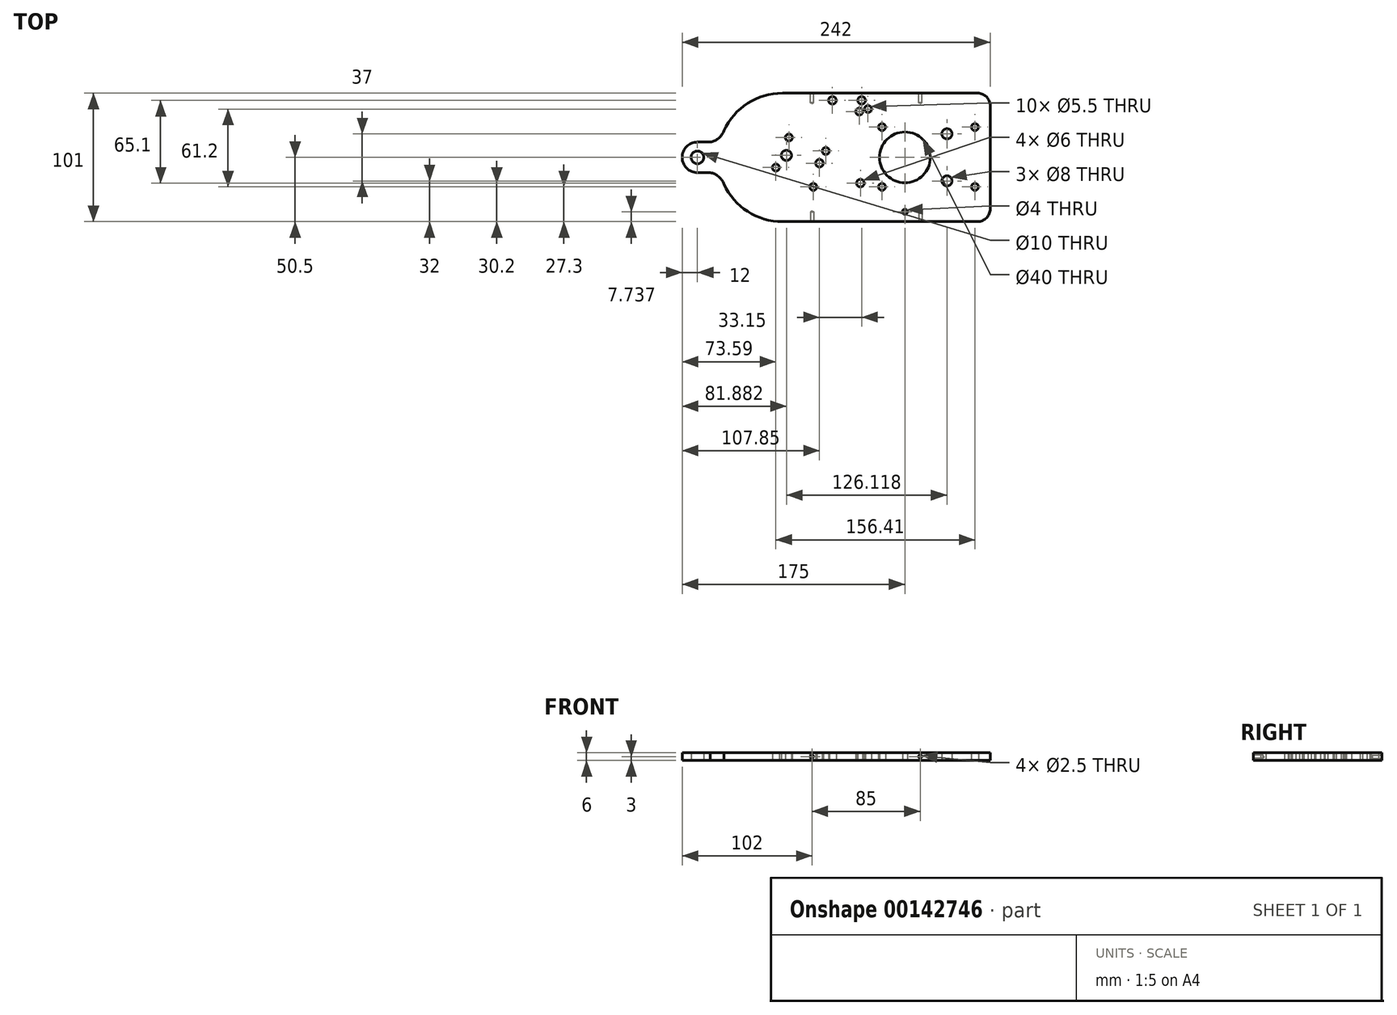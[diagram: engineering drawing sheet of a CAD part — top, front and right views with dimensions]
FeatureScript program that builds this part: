
annotation { "Feature Type Name" : "Feature", "Feature Type Description" : "" }
export const myFeature = defineFeature(function(context is Context, id is Id, definition is map)
    precondition{}
    {
        {
            var Q0;
            Q0=qCreatedBy(makeId("Top.planeOp"),FACE);
            var sketch = newSketch(context, id + "F0", { "sketchPlane" : qUnion([Q0])});
            skCircle(sketch, "E0", {"center": v(0, 0) * mm, "radius": 20 * mm});
            skLineSegment(sketch, "E1.bottom", {"start": v(-96.28, 50.5) * mm, "end": v(57, 50.5) * mm});
            skLineSegment(sketch, "E1.top", {"start": v(-96.28, -50.5) * mm, "end": v(57, -50.5) * mm});
            skLineSegment(sketch, "E1.right", {"start": v(67, 40.5) * mm, "end": v(67, -40.5) * mm});
            skLineSegment(sketch, "E2", {"start": v(-125.63, 0) * mm, "end": v(368.6, 0) * mm, "construction": true});
            skArc(sketch, "E3", {"start": v(-163, 12) * mm, "mid": v(-175, 0) * mm, "end": v(-163, -12) * mm});
            skArc(sketch, "E4", {"start": v(-96.28, 50.5) * mm, "mid": v(-124.3, 42.01) * mm, "end": v(-142.9, 19.41) * mm});
            skLineSegment(sketch, "E5", {"start": v(-163, 0) * mm, "end": v(-153.8, 0) * mm, "construction": true});
            skLineSegment(sketch, "E6", {"start": v(-163, 12) * mm, "end": v(-153, 12) * mm});
            skLineSegment(sketch, "E7", {"start": v(-163, -12) * mm, "end": v(-153, -12) * mm});
            skArc(sketch, "E8", {"start": v(-153, 12) * mm, "mid": v(-146.39, 15.05) * mm, "end": v(-142.2, 21) * mm});
            skArc(sketch, "E9.MirrorCS", {"start": v(-153, -12) * mm, "mid": v(-146.39, -15.05) * mm, "end": v(-142.2, -21) * mm});
            skPoint(sketch, "E10.visualSharp", {"position": v(67, 50.5) * mm});
            skArc(sketch, "E10.filletArc", {"start": v(67, 40.5) * mm, "mid": v(64.07, 47.57) * mm, "end": v(57, 50.5) * mm});
            skPoint(sketch, "E11.visualSharp", {"position": v(67, -50.5) * mm});
            skArc(sketch, "E11.filletArc", {"start": v(57, -50.5) * mm, "mid": v(64.07, -47.57) * mm, "end": v(67, -40.5) * mm});
            skArc(sketch, "E12.trimOffspring", {"start": v(-142.9, -19.41) * mm, "mid": v(-124.3, -42.01) * mm, "end": v(-96.28, -50.5) * mm});
            skCircle(sketch, "E13", {"center": v(-163, 0) * mm, "radius": 5 * mm});
            skCircle(sketch, "E14", {"center": v(33, -18.5) * mm, "radius": 4 * mm});
            skCircle(sketch, "E15", {"center": v(33, 18.5) * mm, "radius": 4 * mm});
            skCircle(sketch, "E16", {"center": v(-57, 44.8) * mm, "radius": 3 * mm});
            skCircle(sketch, "E17", {"center": v(-34, 44.8) * mm, "radius": 3 * mm});
            skCircle(sketch, "E18", {"center": v(-67.15, -4.55) * mm, "radius": 3 * mm});
            skLineSegment(sketch, "E19", {"start": v(0, 0) * mm, "end": v(0, -42.76) * mm, "construction": true});
            skCircle(sketch, "E20", {"center": v(55, 23.8) * mm, "radius": 2.75 * mm});
            skCircle(sketch, "E21", {"center": v(55, -23.2) * mm, "radius": 2.75 * mm});
            skCircle(sketch, "E22", {"center": v(-35.9, 36) * mm, "radius": 2.75 * mm});
            skCircle(sketch, "E23", {"center": v(-29, 38) * mm, "radius": 2.75 * mm});
            skCircle(sketch, "E24", {"center": v(-62.2, 5) * mm, "radius": 2.75 * mm});
            skCircle(sketch, "E25", {"center": v(-91.15, 15.6) * mm, "radius": 2.75 * mm});
            skCircle(sketch, "E26", {"center": v(-93.12, 1.52) * mm, "radius": 4 * mm});
            skCircle(sketch, "E27", {"center": v(-101.4, -8) * mm, "radius": 2.75 * mm});
            skCircle(sketch, "E28", {"center": v(0, -42.76) * mm, "radius": 2 * mm});
            skCircle(sketch, "E29", {"center": v(-35, -20.3) * mm, "radius": 3 * mm});
            skCircle(sketch, "E30", {"center": v(-18, -23.2) * mm, "radius": 2.75 * mm});
            skCircle(sketch, "E31", {"center": v(-72, -23.2) * mm, "radius": 2.75 * mm});
            skCircle(sketch, "E32", {"center": v(-18, 23.8) * mm, "radius": 2.75 * mm});
            skSolve(sketch);
        }
        {
            var Q0;
            Q0=makeQuery(id+"F0.imprint","IMPRINT",FACE,{"disambiguationData":[TD([[makeQuery(id+"F0.imprint","IMPRINT",EDGE,{"derivedFrom":sQuery(id+"F0.wireOp",EDGE,"E0")}),-1.0]])]});
            extrude(context, id + "F1", {"entities" : qUnion([Q0]), "depth" : 6 * mm});
        }
        {
            var Q0;
            Q0=qCreatedBy(makeId("Front.planeOp"),FACE);
            var sketch = newSketch(context, id + "F2", { "sketchPlane" : qUnion([Q0])});
            skLineSegment(sketch, "E33.0", {"start": v(67, 6) * mm, "end": v(67, 0) * mm, "construction": true});
            skPoint(sketch, "E34.endSnap0", {"position": v(67, 3) * mm});
            skCircle(sketch, "E35", {"center": v(-73, 3) * mm, "radius": 1.25 * mm});
            skCircle(sketch, "E36", {"center": v(12, 3) * mm, "radius": 1.25 * mm});
            skSolve(sketch);
        }
        {
            var Q0;
            Q0=makeQuery(id+"F1.opExtrude","SWEPT_FACE",FACE,{"disambiguationData":[OSD([sQuery(id+"F0.wireOp",EDGE,"E1.top")])]});
            var sketch = newSketch(context, id + "F3", { "sketchPlane" : qUnion([Q0])});
            skPoint(sketch, "E37.0", {"position": v(-73, 3) * mm});
            skPoint(sketch, "E38.0", {"position": v(12, 3) * mm});
            skCircle(sketch, "E39", {"center": v(-73, 3) * mm, "radius": 1.25 * mm, "construction": true});
            skCircle(sketch, "E40", {"center": v(12, 3) * mm, "radius": 1.25 * mm, "construction": true});
            skSolve(sketch);
        }
        {
            var Q0;
            Q0=sQuery(id+"F3.wireOp",VERTEX,"E37.0");
            var Q1;
            Q1=sQuery(id+"F3.wireOp",VERTEX,"E38.0");
            var Q2;
            Q2=makeQuery(id+"F1.opExtrude","SWEPT_BODY",BODY,{"disambiguationData":[OSD([sQuery(id+"F0.wireOp",EDGE,"E0"),sQuery(id+"F0.wireOp",EDGE,"E1.bottom"),sQuery(id+"F0.wireOp",EDGE,"E1.top"),sQuery(id+"F0.wireOp",EDGE,"E1.right"),sQuery(id+"F0.wireOp",EDGE,"E3"),sQuery(id+"F0.wireOp",EDGE,"E4"),sQuery(id+"F0.wireOp",EDGE,"E6"),sQuery(id+"F0.wireOp",EDGE,"E7"),sQuery(id+"F0.wireOp",EDGE,"E8"),sQuery(id+"F0.wireOp",EDGE,"E9.MirrorCS"),sQuery(id+"F0.wireOp",EDGE,"E10.filletArc"),sQuery(id+"F0.wireOp",EDGE,"E11.filletArc"),sQuery(id+"F0.wireOp",EDGE,"E12.trimOffspring"),sQuery(id+"F0.wireOp",EDGE,"E13"),sQuery(id+"F0.wireOp",EDGE,"E14"),sQuery(id+"F0.wireOp",EDGE,"E15"),sQuery(id+"F0.wireOp",EDGE,"E16"),sQuery(id+"F0.wireOp",EDGE,"E17"),sQuery(id+"F0.wireOp",EDGE,"E18"),sQuery(id+"F0.wireOp",EDGE,"E20"),sQuery(id+"F0.wireOp",EDGE,"E21"),sQuery(id+"F0.wireOp",EDGE,"E22"),sQuery(id+"F0.wireOp",EDGE,"E23"),sQuery(id+"F0.wireOp",EDGE,"E24"),sQuery(id+"F0.wireOp",EDGE,"E25"),sQuery(id+"F0.wireOp",EDGE,"E26"),sQuery(id+"F0.wireOp",EDGE,"E27"),sQuery(id+"F0.wireOp",EDGE,"E28"),sQuery(id+"F0.wireOp",EDGE,"E29"),sQuery(id+"F0.wireOp",EDGE,"E30"),sQuery(id+"F0.wireOp",EDGE,"E31"),sQuery(id+"F0.wireOp",EDGE,"E32")])]});
            hole(context, id + "F4", {"style" : HoleStyle.SIMPLE, "endStyle" : HoleEndStyle.BLIND, "holeDiameter" : 2.5 * mm, "holeDepth" : 7.6 * mm, "locations" : qUnion([Q0, Q1]), "scope" : qUnion([Q2])});
        }
        {
            var Q0;
            Q0=qCreatedBy(makeId("Front.planeOp"),FACE);
            var sketch = newSketch(context, id + "F5", { "sketchPlane" : qUnion([Q0])});
            skPoint(sketch, "E41.0", {"position": v(12, 3) * mm});
            skPoint(sketch, "E42.0", {"position": v(-73, 3) * mm});
            skCircle(sketch, "E43", {"center": v(-73, 3) * mm, "radius": 1.25 * mm});
            skCircle(sketch, "E44", {"center": v(12, 3) * mm, "radius": 1.25 * mm});
            skSolve(sketch);
        }
        {
            var Q0;
            Q0=makeQuery(id+"F1.opExtrude","SWEPT_FACE",FACE,{"disambiguationData":[OSD([sQuery(id+"F0.wireOp",EDGE,"E1.bottom")])]});
            var sketch = newSketch(context, id + "F6", { "sketchPlane" : qUnion([Q0])});
            skPoint(sketch, "E45.0", {"position": v(-12, 3) * mm});
            skPoint(sketch, "E46.0", {"position": v(73, 3) * mm});
            skCircle(sketch, "E47", {"center": v(-12, 3) * mm, "radius": 1.25 * mm});
            skCircle(sketch, "E48", {"center": v(73, 3) * mm, "radius": 1.25 * mm});
            skSolve(sketch);
        }
        {
            var Q0;
            Q0=sQuery(id+"F6.wireOp",VERTEX,"E45.0");
            var Q1;
            Q1=sQuery(id+"F6.wireOp",VERTEX,"E46.0");
            var Q2;
            Q2=makeQuery(id+"F1.opExtrude","SWEPT_BODY",BODY,{"disambiguationData":[OSD([sQuery(id+"F0.wireOp",EDGE,"E0"),sQuery(id+"F0.wireOp",EDGE,"E1.bottom"),sQuery(id+"F0.wireOp",EDGE,"E1.top"),sQuery(id+"F0.wireOp",EDGE,"E1.right"),sQuery(id+"F0.wireOp",EDGE,"E3"),sQuery(id+"F0.wireOp",EDGE,"E4"),sQuery(id+"F0.wireOp",EDGE,"E6"),sQuery(id+"F0.wireOp",EDGE,"E7"),sQuery(id+"F0.wireOp",EDGE,"E8"),sQuery(id+"F0.wireOp",EDGE,"E9.MirrorCS"),sQuery(id+"F0.wireOp",EDGE,"E10.filletArc"),sQuery(id+"F0.wireOp",EDGE,"E11.filletArc"),sQuery(id+"F0.wireOp",EDGE,"E12.trimOffspring"),sQuery(id+"F0.wireOp",EDGE,"E13"),sQuery(id+"F0.wireOp",EDGE,"E14"),sQuery(id+"F0.wireOp",EDGE,"E15"),sQuery(id+"F0.wireOp",EDGE,"E16"),sQuery(id+"F0.wireOp",EDGE,"E17"),sQuery(id+"F0.wireOp",EDGE,"E18"),sQuery(id+"F0.wireOp",EDGE,"E20"),sQuery(id+"F0.wireOp",EDGE,"E21"),sQuery(id+"F0.wireOp",EDGE,"E22"),sQuery(id+"F0.wireOp",EDGE,"E23"),sQuery(id+"F0.wireOp",EDGE,"E24"),sQuery(id+"F0.wireOp",EDGE,"E25"),sQuery(id+"F0.wireOp",EDGE,"E26"),sQuery(id+"F0.wireOp",EDGE,"E27"),sQuery(id+"F0.wireOp",EDGE,"E28"),sQuery(id+"F0.wireOp",EDGE,"E29"),sQuery(id+"F0.wireOp",EDGE,"E30"),sQuery(id+"F0.wireOp",EDGE,"E31"),sQuery(id+"F0.wireOp",EDGE,"E32")])]});
            hole(context, id + "F7", {"style" : HoleStyle.SIMPLE, "endStyle" : HoleEndStyle.BLIND, "holeDiameter" : 2.5 * mm, "holeDepth" : 7.6 * mm, "locations" : qUnion([Q0, Q1]), "scope" : qUnion([Q2])});
        }
    });
